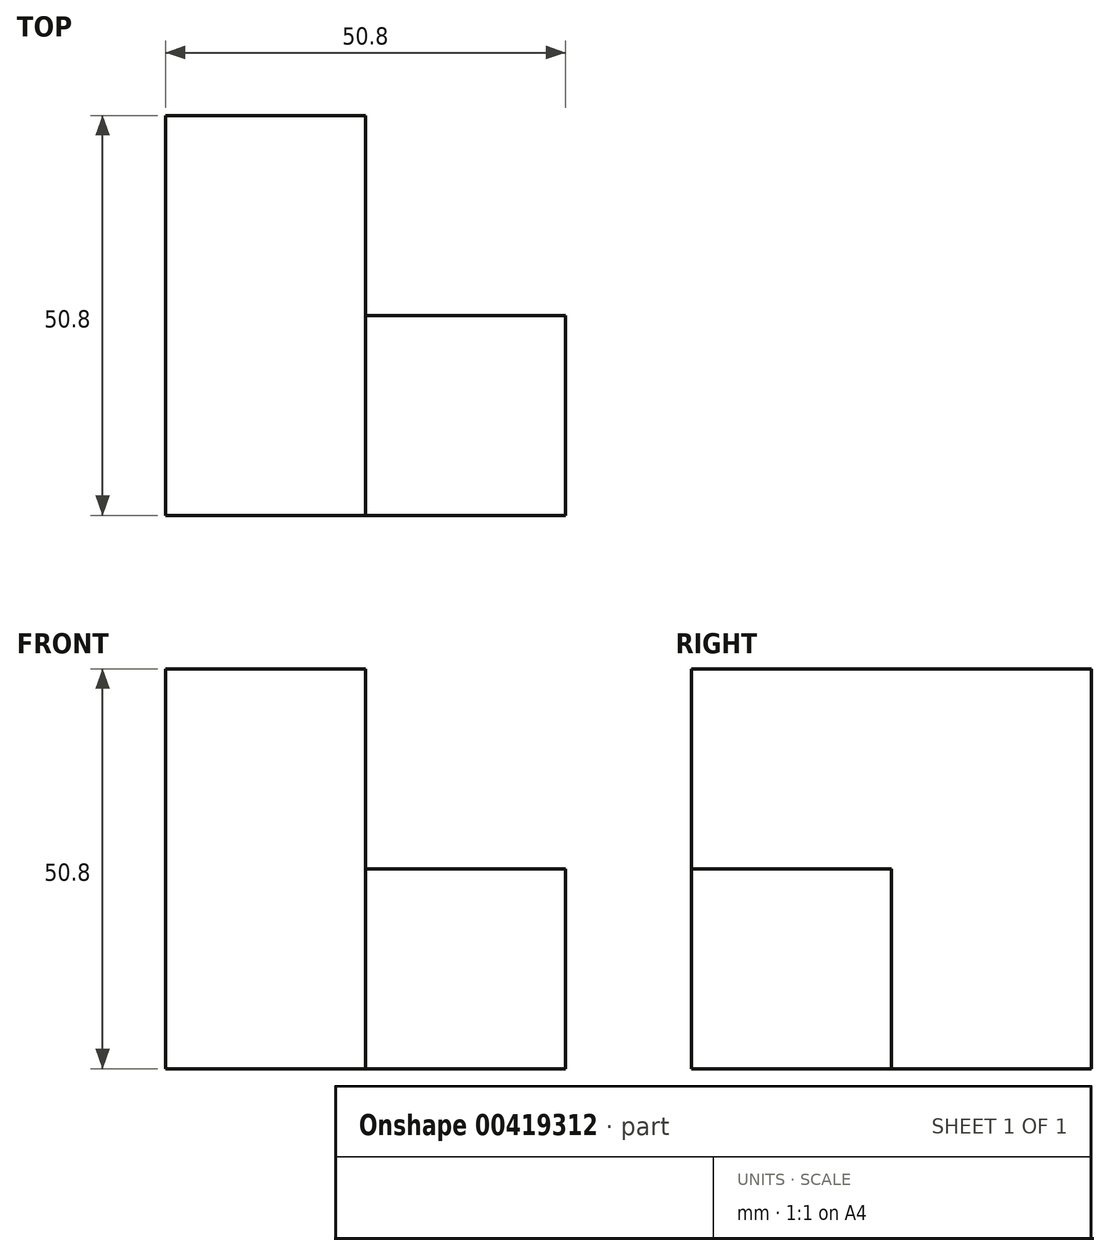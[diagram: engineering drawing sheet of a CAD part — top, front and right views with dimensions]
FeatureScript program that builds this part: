
annotation { "Feature Type Name" : "Feature", "Feature Type Description" : "" }
export const myFeature = defineFeature(function(context is Context, id is Id, definition is map)
    precondition{}
    {
        {
            var Q0;
            Q0=qCreatedBy(makeId("Front.planeOp"),FACE);
            var sketch = newSketch(context, id + "F0", { "sketchPlane" : qUnion([Q0])});
            skLineSegment(sketch, "E0.bottom", {"start": v(0, 0) * mm, "end": v(-25.4, 0) * mm});
            skLineSegment(sketch, "E0.top", {"start": v(0, 50.8) * mm, "end": v(-25.4, 50.8) * mm});
            skLineSegment(sketch, "E0.left", {"start": v(0, 0) * mm, "end": v(0, 50.8) * mm});
            skLineSegment(sketch, "E0.right", {"start": v(-25.4, 0) * mm, "end": v(-25.4, 50.8) * mm});
            skSolve(sketch);
        }
        {
            var Q0;
            Q0 = qSketchRegion(id + "F0", true);
            extrude(context, id + "F1", {"entities" : qUnion([Q0]), "depth" : 50.8 * mm});
        }
        {
            var Q0;
            Q0=makeQuery(id+"F1.opExtrude","SWEPT_FACE",FACE,{"disambiguationData":[OSD([sQuery(id+"F0.wireOp",EDGE,"E0.left")])]});
            var sketch = newSketch(context, id + "F2", { "sketchPlane" : qUnion([Q0])});
            skLineSegment(sketch, "E1.bottom", {"start": v(-50.8, 25.4) * mm, "end": v(-25.4, 25.4) * mm});
            skLineSegment(sketch, "E1.top", {"start": v(-50.8, 0) * mm, "end": v(-25.4, 0) * mm});
            skLineSegment(sketch, "E1.left", {"start": v(-50.8, 25.4) * mm, "end": v(-50.8, 0) * mm});
            skLineSegment(sketch, "E1.right", {"start": v(-25.4, 25.4) * mm, "end": v(-25.4, 0) * mm});
            skSolve(sketch);
        }
        {
            var Q0;
            Q0 = qSketchRegion(id + "F2", true);
            extrude(context, id + "F3", {"entities" : qUnion([Q0]), "depth" : 25.4 * mm});
        }
    });
